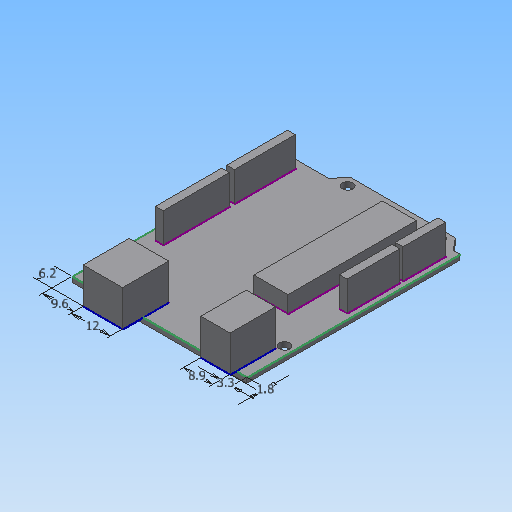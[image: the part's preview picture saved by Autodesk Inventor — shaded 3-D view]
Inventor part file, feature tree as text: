
AUTODESK INVENTOR PART (.ipt)
format: ipt  version: 2017 (Build 210142000, 142)  size: 158,720 bytes
history: native  units: in
note: dims shown in document units (in); Inventor stores cm internally (conversion verified against a paired STEP export)
features: extrude x4, sketch x2
ambient origin geometry x8: Origin, YZ Plane, XZ Plane, XY Plane, X Axis, Y Axis, Z Axis, Center Point
bodies: Solid1 (feature_tree)
feature tree (6):
  extrude  "board"  Depth=2.0984in
  sketch  "Sketch2"  dims[d6=0.0433in d8=1.0984in d9=0.5984in d10=2.7008in d11=0.126in d12=2.0in d13=0.185in d15=0.0984in d17=0.5512in d18=1.4567in d19=1.5748in d20=0.0787in d21=0.1969in d22=2.5591in d23=0.063in d24=0.0in d25=0.378in d26=0.4724in d27=0.1299in d28=0.3504in d29=0.0709in d30=0.2441in d31=0.4291in d32=0.0in d33=0.1969in d34=0.0in d35=0.3543in d36=0.0in]
  extrude  "Extrusion2"  Depth=0.3543in
  extrude  "Extrusion3"  Depth=0.3543in
  extrude  "Extrusion4"  Depth=2.7008in
  sketch  "Sketch1"  dims[d2=2.0984in d5=2.0433in]
